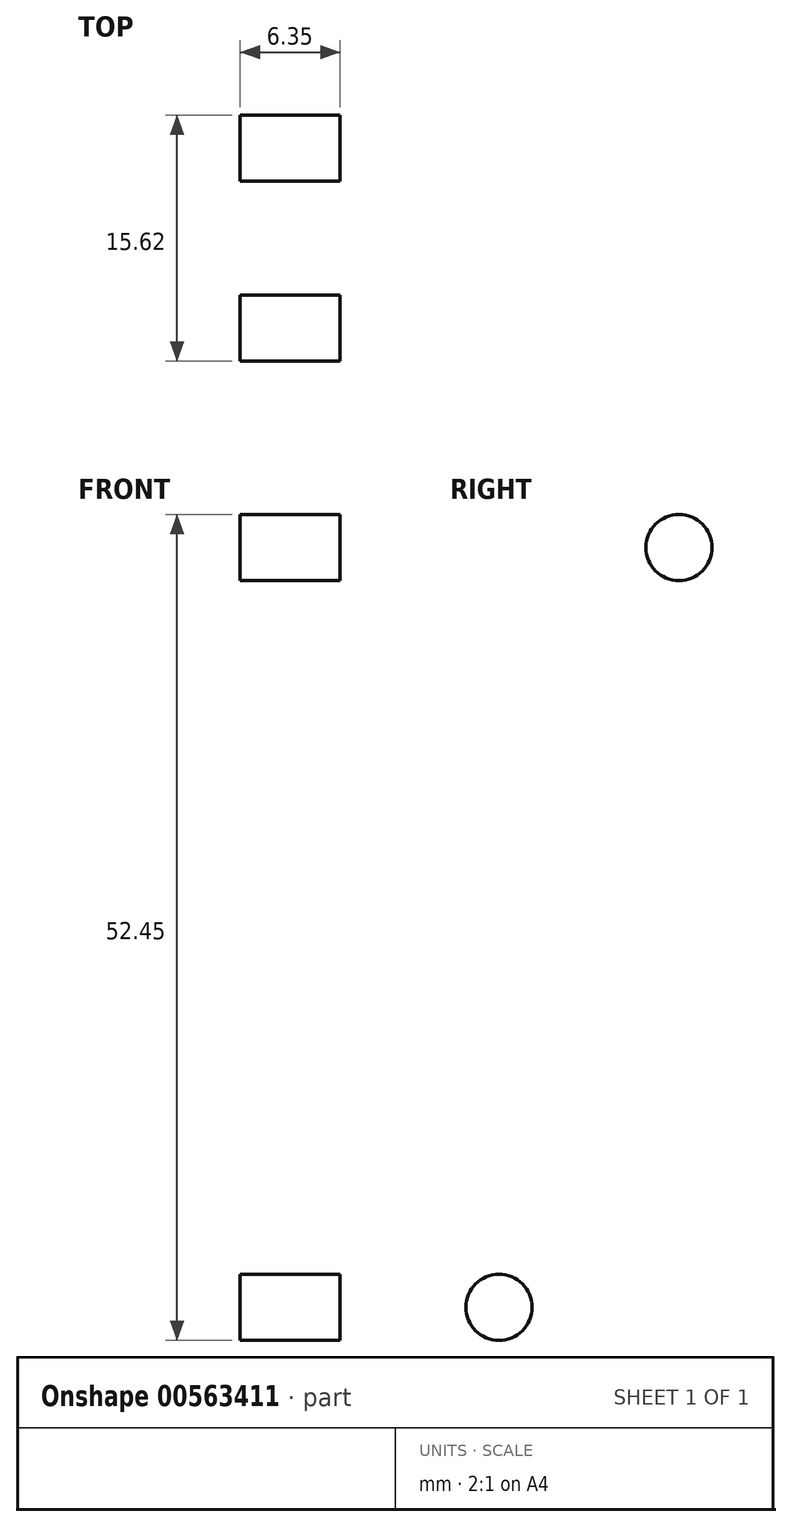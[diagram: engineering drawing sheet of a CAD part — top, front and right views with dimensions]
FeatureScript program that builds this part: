
annotation { "Feature Type Name" : "Feature", "Feature Type Description" : "" }
export const myFeature = defineFeature(function(context is Context, id is Id, definition is map)
    precondition{}
    {
        {
            var Q0;
            Q0=qCreatedBy(makeId("Right.planeOp"),FACE);
            var sketch = newSketch(context, id + "F0", { "sketchPlane" : qUnion([Q0])});
            skLineSegment(sketch, "E0", {"start": v(0, 0) * mm, "end": v(101.6, 0) * mm});
            skLineSegment(sketch, "E1", {"start": v(50.8, 0) * mm, "end": v(50.8, -101.6) * mm});
            skArc(sketch, "E2", {"start": v(50.8, -101.6) * mm, "mid": v(70.26, -98.06) * mm, "end": v(87.22, -87.9) * mm});
            skArc(sketch, "E3.MirrorCS", {"start": v(50.8, -101.6) * mm, "mid": v(31.34, -98.06) * mm, "end": v(14.38, -87.9) * mm});
            skLineSegment(sketch, "E4", {"start": v(101.6, 0) * mm, "end": v(101.6, -6.35) * mm});
            skLineSegment(sketch, "E5", {"start": v(101.6, -6.35) * mm, "end": v(87.22, -87.9) * mm});
            skLineSegment(sketch, "E6.MirrorCS", {"start": v(0, -6.35) * mm, "end": v(14.38, -87.9) * mm});
            skLineSegment(sketch, "E7.MirrorCS", {"start": v(0, 0) * mm, "end": v(0, -6.35) * mm});
            skSolve(sketch);
        }
        {
            var Q0;
            {var subQ2=sQuery(id+"F0.wireOp",EDGE,"E1");Q0=makeQuery(id+"F0.imprint","IMPRINT",FACE,{"disambiguationData":[TD([[makeQuery(id+"F0.imprint","IMPRINT",EDGE,{"derivedFrom":subQ2}),-1.0]])]});}
            var Q1;
            {var subQ0=sQuery(id+"F0.wireOp",EDGE,"khOB3p5o-ioRN-m1G3-Y8gc-wrssJ04mrUhv");Q1=makeQuery(id+"F0.imprint","IMPRINT",FACE,{"disambiguationData":[TD([[makeQuery(id+"F0.imprint","IMPRINT",EDGE,{"derivedFrom":subQ0}),-1.0]])]});}
            var Q2;
            {var subQ1=sQuery(id+"F0.wireOp",EDGE,"E1");Q2=makeQuery(id+"F0.imprint","IMPRINT",FACE,{"disambiguationData":[TD([[makeQuery(id+"F0.imprint","IMPRINT",EDGE,{"derivedFrom":subQ1}),1.0]])]});}
            extrude(context, id + "F1", {"entities" : qUnion([Q0, Q1, Q2]), "depth" : 6.35 * mm, "offsetDistance" : 25.4 * mm});
        }
        {
            var Q0;
            Q0=makeQuery(id+"F1.opExtrude","CAP_FACE",FACE,{"disambiguationData":[OSD([sQuery(id+"F0.wireOp",EDGE,"E0"),sQuery(id+"F0.wireOp",EDGE,"khOB3p5o-ioRN-m1G3-Y8gc-wrssJ04mrUhv"),sQuery(id+"F0.wireOp",EDGE,"E2"),sQuery(id+"F0.wireOp",EDGE,"4d74da0e-6006-49e8-a9db-5cfd90e2330b0.MirrorCS"),sQuery(id+"F0.wireOp",EDGE,"E3.MirrorCS")])],"isStart":false});
            var sketch = newSketch(context, id + "F2", { "sketchPlane" : qUnion([Q0])});
            skLineSegment(sketch, "E8.top", {"start": v(12.7, -6.35) * mm, "end": v(38.1, -6.35) * mm});
            skLineSegment(sketch, "E8.left", {"start": v(12.7, 0) * mm, "end": v(12.7, -6.35) * mm});
            skLineSegment(sketch, "E8.right", {"start": v(38.1, 0) * mm, "end": v(38.1, -6.35) * mm});
            skLineSegment(sketch, "E9", {"start": v(50.8, 0) * mm, "end": v(50.8, -101.6) * mm});
            skLineSegment(sketch, "E10.MirrorCS", {"start": v(63.5, 0) * mm, "end": v(63.5, -6.35) * mm});
            skLineSegment(sketch, "E11.MirrorCS", {"start": v(88.9, 0) * mm, "end": v(88.9, -6.35) * mm});
            skLineSegment(sketch, "E12.MirrorCS", {"start": v(88.9, -6.35) * mm, "end": v(63.5, -6.35) * mm});
            skLineSegment(sketch, "E13", {"start": v(12.7, -6.35) * mm, "end": v(0, -6.35) * mm});
            skLineSegment(sketch, "E14", {"start": v(0, -6.35) * mm, "end": v(0, 0) * mm});
            skLineSegment(sketch, "E15", {"start": v(0, 0) * mm, "end": v(12.7, 0) * mm});
            skLineSegment(sketch, "E16", {"start": v(38.1, -6.35) * mm, "end": v(63.5, -6.35) * mm});
            skLineSegment(sketch, "E17", {"start": v(88.9, -6.35) * mm, "end": v(101.6, -6.35) * mm});
            skLineSegment(sketch, "E18", {"start": v(101.6, -6.35) * mm, "end": v(101.6, 0) * mm});
            skLineSegment(sketch, "E19", {"start": v(101.6, 0) * mm, "end": v(88.9, 0) * mm});
            skLineSegment(sketch, "E20", {"start": v(38.1, 0) * mm, "end": v(63.5, 0) * mm});
            skSolve(sketch);
        }
        {
            var Q0;
            Q0 = qSketchRegion(id + "F2", true);
            extrude(context, id + "F3", {"entities" : qUnion([Q0]), "operationType" : NewBodyOperationType.REMOVE, "oppositeDirection" : true, "depth" : 25.4 * mm, "offsetDistance" : 25.4 * mm});
        }
        {
            var Q0;
            Q0=makeQuery(id+"F1.opExtrude","CAP_FACE",FACE,{"disambiguationData":[OSD([sQuery(id+"F0.wireOp",EDGE,"E0"),sQuery(id+"F0.wireOp",EDGE,"E2"),sQuery(id+"F0.wireOp",EDGE,"E3.MirrorCS"),sQuery(id+"F0.wireOp",EDGE,"E4"),sQuery(id+"F0.wireOp",EDGE,"E5"),sQuery(id+"F0.wireOp",EDGE,"E6.MirrorCS"),sQuery(id+"F0.wireOp",EDGE,"E7.MirrorCS")])],"isStart":false});
            var sketch = newSketch(context, id + "F4", { "sketchPlane" : qUnion([Q0])});
            skLineSegment(sketch, "E21.bottom", {"start": v(39.78, -46.99) * mm, "end": v(60.1, -46.99) * mm});
            skLineSegment(sketch, "E21.top", {"start": v(39.78, -87) * mm, "end": v(60.1, -87) * mm});
            skLineSegment(sketch, "E21.left", {"start": v(39.78, -46.99) * mm, "end": v(39.78, -87) * mm});
            skLineSegment(sketch, "E21.right", {"start": v(60.1, -46.99) * mm, "end": v(60.1, -87) * mm});
            skCircle(sketch, "E22", {"center": v(44.22, -42.86) * mm, "radius": 2.1 * mm});
            skCircle(sketch, "E23.MirrorC", {"center": v(55.65, -42.86) * mm, "radius": 2.1 * mm});
            skCircle(sketch, "E24.MirrorC", {"center": v(55.65, -91.12) * mm, "radius": 2.1 * mm});
            skCircle(sketch, "E25.MirrorC", {"center": v(44.22, -91.12) * mm, "radius": 2.1 * mm});
            skSolve(sketch);
        }
        {
            var Q0;
            Q0=makeQuery(id+"F4.imprint","IMPRINT",FACE,{"disambiguationData":[TD([[makeQuery(id+"F4.imprint","IMPRINT",EDGE,{"derivedFrom":sQuery(id+"F4.wireOp",EDGE,"E21.bottom")}),-1.0]])]});
            var Q1;
            Q1=makeQuery(id+"F4.imprint","IMPRINT",FACE,{"disambiguationData":[TD([[makeQuery(id+"F4.imprint","IMPRINT",EDGE,{"derivedFrom":sQuery(id+"F4.wireOp",EDGE,"E22")}),1.0]])]});
            var Q2;
            Q2=makeQuery(id+"F4.imprint","IMPRINT",FACE,{"disambiguationData":[TD([[makeQuery(id+"F4.imprint","IMPRINT",EDGE,{"derivedFrom":sQuery(id+"F4.wireOp",EDGE,"E23.MirrorC")}),-1.0]])]});
            var Q3;
            Q3=makeQuery(id+"F4.imprint","IMPRINT",FACE,{"disambiguationData":[TD([[makeQuery(id+"F4.imprint","IMPRINT",EDGE,{"derivedFrom":sQuery(id+"F4.wireOp",EDGE,"E24.MirrorC")}),1.0]])]});
            var Q4;
            Q4=makeQuery(id+"F4.imprint","IMPRINT",FACE,{"disambiguationData":[TD([[makeQuery(id+"F4.imprint","IMPRINT",EDGE,{"derivedFrom":sQuery(id+"F4.wireOp",EDGE,"E25.MirrorC")}),-1.0]])]});
            extrude(context, id + "F5", {"entities" : qUnion([Q0, Q1, Q2, Q3, Q4]), "operationType" : NewBodyOperationType.REMOVE, "oppositeDirection" : true, "depth" : 25.4 * mm, "offsetDistance" : 25.4 * mm});
        }
    });
